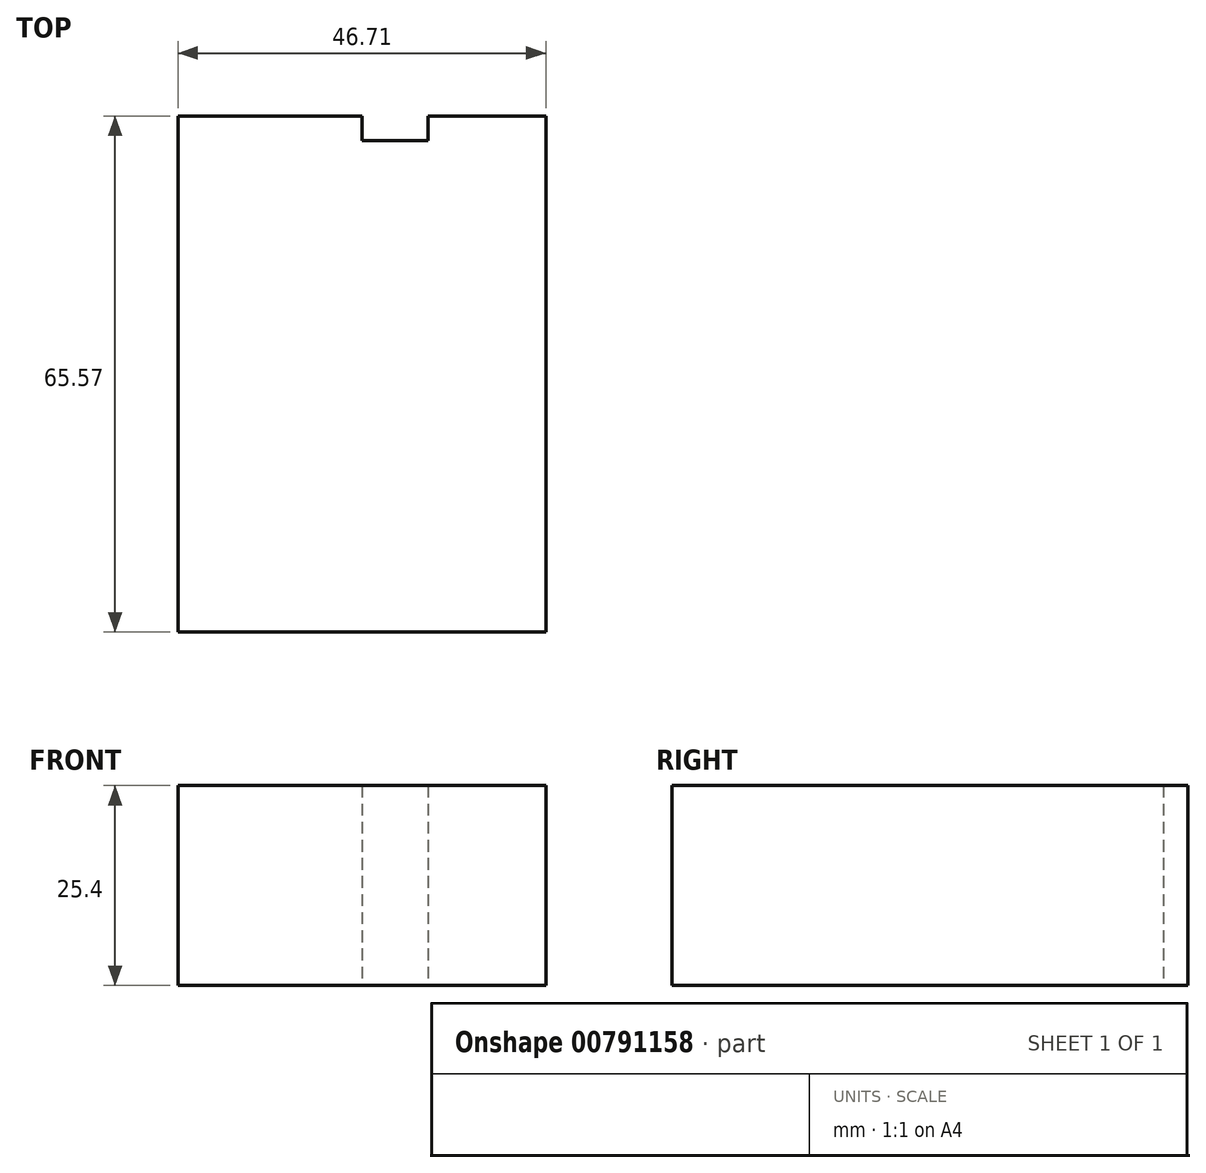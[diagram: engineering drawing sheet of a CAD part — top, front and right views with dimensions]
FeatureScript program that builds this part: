
annotation { "Feature Type Name" : "Feature", "Feature Type Description" : "" }
export const myFeature = defineFeature(function(context is Context, id is Id, definition is map)
    precondition{}
    {
        {
            var Q0;
            Q0=qCreatedBy(makeId("Top.planeOp"),FACE);
            var sketch = newSketch(context, id + "F0", { "sketchPlane" : qUnion([Q0])});
            skLineSegment(sketch, "E0.bottom", {"start": v(-46.7, 65.57) * mm, "end": v(0, 65.57) * mm});
            skLineSegment(sketch, "E0.top", {"start": v(-46.7, 0) * mm, "end": v(0, 0) * mm});
            skLineSegment(sketch, "E0.left", {"start": v(-46.7, 65.57) * mm, "end": v(-46.7, 0) * mm});
            skLineSegment(sketch, "E0.right", {"start": v(0, 65.57) * mm, "end": v(0, 0) * mm});
            skLineSegment(sketch, "E1.bottom", {"start": v(-23.35, 65.57) * mm, "end": v(-14.96, 65.57) * mm});
            skLineSegment(sketch, "E1.top", {"start": v(-23.35, 62.45) * mm, "end": v(-14.96, 62.45) * mm});
            skLineSegment(sketch, "E1.left", {"start": v(-23.35, 65.57) * mm, "end": v(-23.35, 62.45) * mm});
            skLineSegment(sketch, "E1.right", {"start": v(-14.96, 65.57) * mm, "end": v(-14.96, 62.45) * mm});
            skSolve(sketch);
        }
        {
            var Q0;
            Q0=makeQuery(id+"F0.imprint","IMPRINT",FACE,{"disambiguationData":[TD([[makeQuery(id+"F0.imprint","IMPRINT",EDGE,{"derivedFrom":sQuery(id+"F0.wireOp",EDGE,"E0.top")}),1.0]])]});
            extrude(context, id + "F1", {"entities" : qUnion([Q0]), "depth" : 25.4 * mm, "offsetDistance" : 25.4 * mm});
        }
    });
